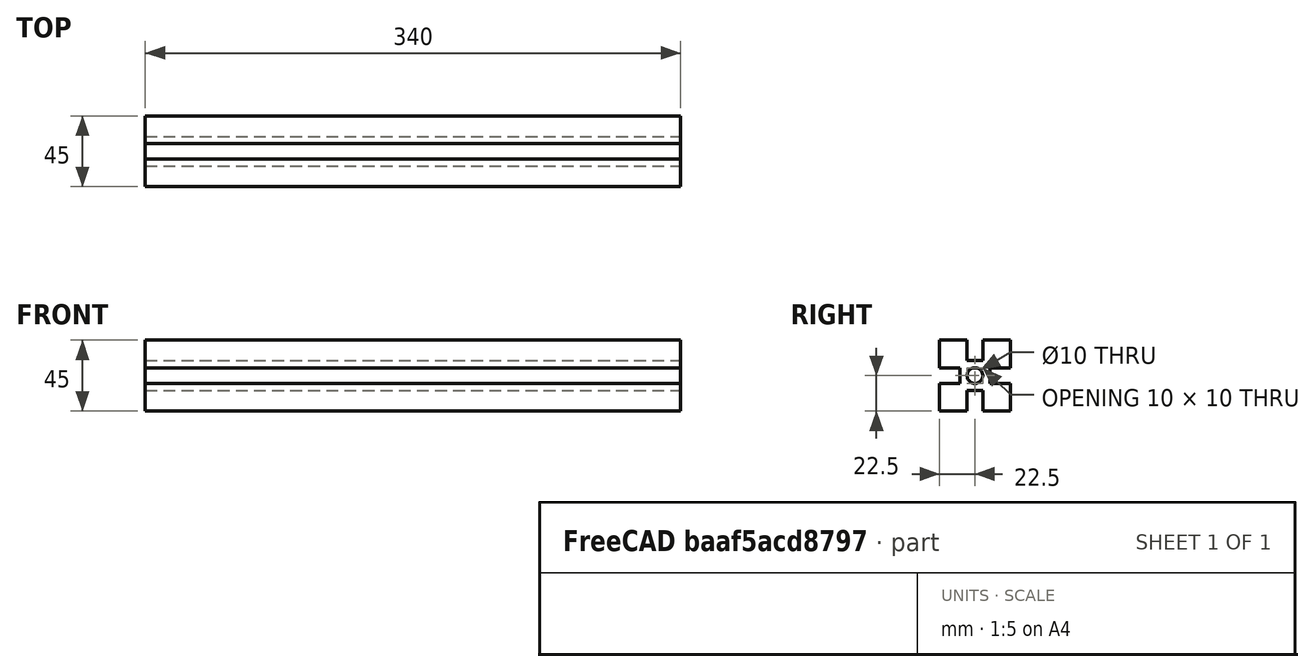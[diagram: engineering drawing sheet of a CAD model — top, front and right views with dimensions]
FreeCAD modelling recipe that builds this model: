
FCSTD DOCUMENT  (FreeCAD 1.0R39109 (Git))
Label: vslot 45x45x340
License: All rights reserved
LicenseURL: https://en.wikipedia.org/wiki/All_rights_reserved
objects: PartDesign::Pocket×4, PartDesign::Pad×2, Part::Feature×1, PartDesign::FeatureBase×1, PartDesign::Body×1
note: 22 computed .brp shape members not serialized (recipe doc carries the construction recipe); baked Part::Feature solids carry a one-line shape summary decoded from their .brp

FEATURE [Part::Feature] Part__Feature  label="1"
  shape: bbox 1000 x 45 x 45 mm, 24 faces (baked)
FEATURE [PartDesign::FeatureBase] BaseFeature
  BaseFeature = -> Part__Feature
  Suppressed = false
FEATURE [PartDesign::Pad] Pad
  BaseFeature = -> BaseFeature
  Direction = (1,0,0)
  Length = 220
  Length2 = 10
  Profile = -> BaseFeature [Face24]
  Refine = true
  Suppressed = false
  Type = 0
FEATURE [PartDesign::Pocket] Pocket
  BaseFeature = -> Pad
  Direction = (-1,0,0)
  Length = 140
  Length2 = 5
  Profile = -> Pad [Face3]
  Refine = true
  Suppressed = false
  Type = 0
FEATURE [PartDesign::Pocket] Pocket001
  BaseFeature = -> Pocket
  Direction = (-1,0,0)
  Length = 480
  Length2 = 5
  Profile = -> Pocket [Face23]
  Refine = true
  Suppressed = false
  Type = 0
FEATURE [PartDesign::Pocket] Pocket002
  BaseFeature = -> Pocket001
  Direction = (-1,0,0)
  Length = 195
  Length2 = 5
  Profile = -> Pocket001 [Face23]
  Refine = true
  Suppressed = false
  Type = 0
FEATURE [PartDesign::Pocket] Pocket003
  BaseFeature = -> Pocket002
  Direction = (-1,0,0)
  Length = 310
  Length2 = 5
  Profile = -> Pocket002 [Face23]
  Refine = true
  Suppressed = false
  Type = 0
FEATURE [PartDesign::Pad] Pad001
  BaseFeature = -> Pocket003
  Direction = (1,0,0)
  Length = 245
  Length2 = 10
  Profile = -> Pocket003 [Face23]
  Refine = true
  Suppressed = false
  Type = 0
FEATURE [PartDesign::Body] Body
  AllowCompound = false
  BaseFeature = -> Part__Feature
  Group = -> [BaseFeature,Pad,Pocket,Pocket001,Pocket002,Pocket003,Pad001]
  Origin = -> Origin
  Tip = -> Pad001
